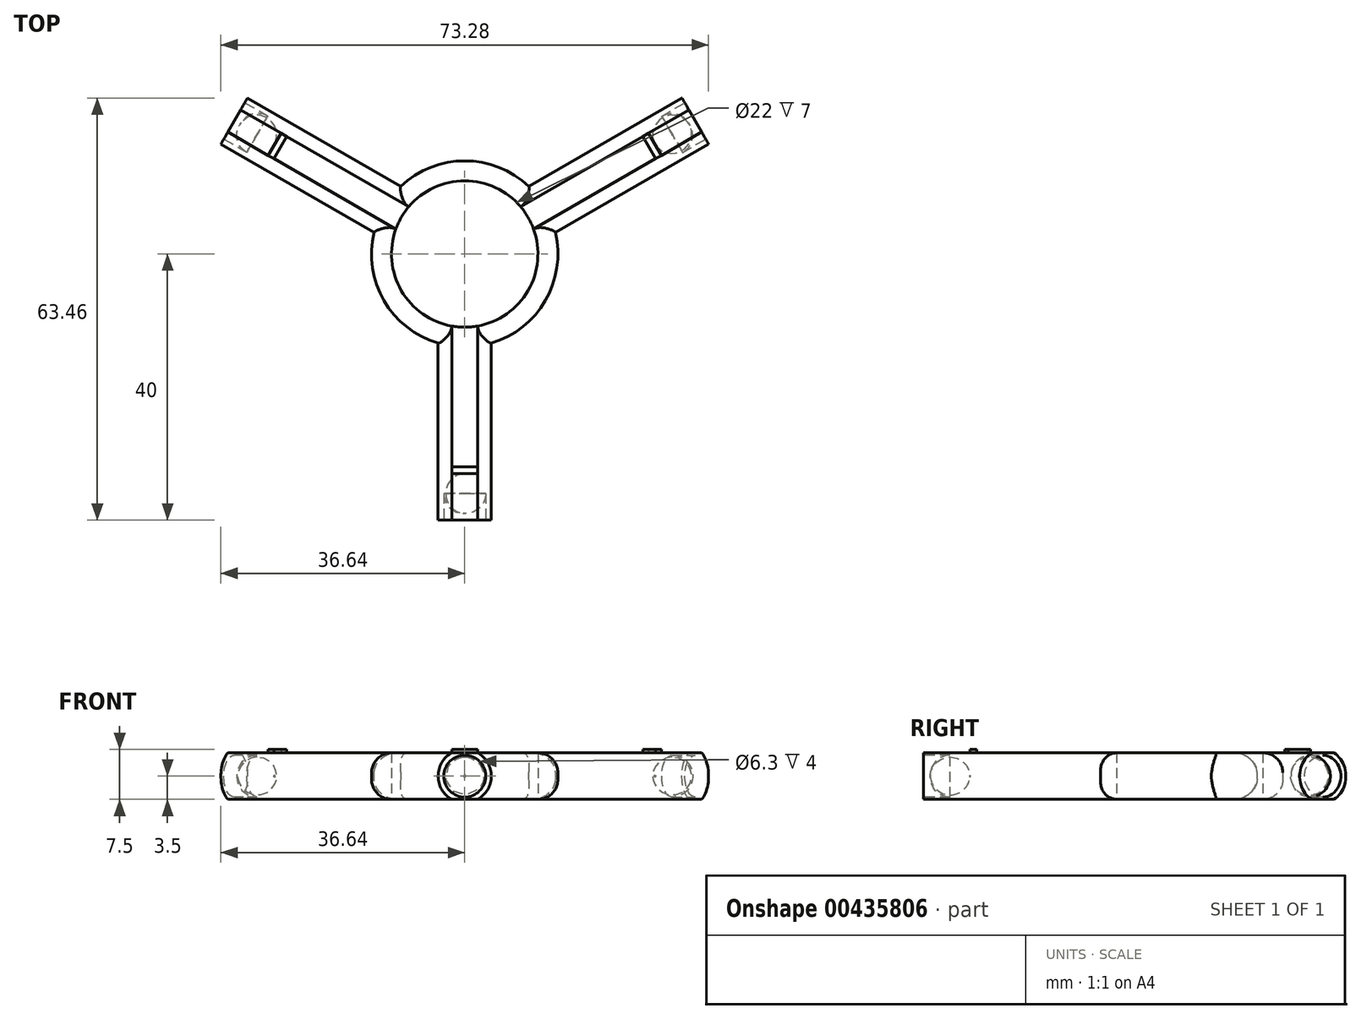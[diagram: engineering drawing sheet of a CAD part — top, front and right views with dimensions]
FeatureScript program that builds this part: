
annotation { "Feature Type Name" : "Feature", "Feature Type Description" : "" }
export const myFeature = defineFeature(function(context is Context, id is Id, definition is map)
    precondition{}
    {
        {
            var Q0;
            Q0=qCreatedBy(makeId("Top.planeOp"),FACE);
            var sketch = newSketch(context, id + "F0", { "sketchPlane" : qUnion([Q0])});
            skCircle(sketch, "E0", {"center": v(0, 0) * mm, "radius": 11 * mm});
            skCircle(sketch, "E1.0", {"center": v(0, 0) * mm, "radius": 14 * mm});
            skSolve(sketch);
        }
        {
            var Q0;
            Q0=makeQuery(id+"F0.imprint","IMPRINT",FACE,{"disambiguationData":[TD([[makeQuery(id+"F0.imprint","IMPRINT",EDGE,{"derivedFrom":sQuery(id+"F0.wireOp",EDGE,"E0")}),-1.0]])]});
            extrude(context, id + "F1", {"entities" : qUnion([Q0]), "depth" : 7 * mm, "offsetDistance" : 25 * mm});
        }
        {
            var Q0;
            Q0=qCreatedBy(makeId("Front.planeOp"),FACE);
            var sketch = newSketch(context, id + "F2", { "sketchPlane" : qUnion([Q0])});
            skCircle(sketch, "E2", {"center": v(0, 3.5) * mm, "radius": 4 * mm});
            skLineSegment(sketch, "E3", {"start": v(1.94, 7) * mm, "end": v(-1.94, 7) * mm});
            skLineSegment(sketch, "E4", {"start": v(1.94, 0) * mm, "end": v(-1.94, 0) * mm});
            skSolve(sketch);
        }
        {
            var Q0;
            {var subQ0=sQuery(id+"F2.wireOp",EDGE,"E3");Q0=makeQuery(id+"F2.imprint","IMPRINT",FACE,{"disambiguationData":[TD([[makeQuery(id+"F2.imprint","IMPRINT",EDGE,{"derivedFrom":subQ0}),1.0]])]});}
            extrude(context, id + "F3", {"entities" : qUnion([Q0]), "operationType" : NewBodyOperationType.ADD, "depth" : 40 * mm, "offsetDistance" : 25 * mm, "hasSecondDirection" : true, "secondDirectionBound" : SecondDirectionBoundingType.UP_TO_NEXT, "secondDirectionOppositeDirection" : false, "secondDirectionDepth" : 9.3 * mm});
        }
        {
            var Q0;
            Q0=makeQuery(id+"F3.opExtrude","CAP_FACE",FACE,{"disambiguationData":[OSD([sQuery(id+"F2.wireOp",EDGE,"E2"),sQuery(id+"F2.wireOp",EDGE,"E3"),sQuery(id+"F2.wireOp",EDGE,"E4")])],"isStart":false});
            var sketch = newSketch(context, id + "F4", { "sketchPlane" : qUnion([Q0])});
            skCircle(sketch, "E5", {"center": v(0, 3.5) * mm, "radius": 3.15 * mm});
            skCircle(sketch, "E6", {"center": v(0, 3.5) * mm, "radius": 4 * mm, "construction": true});
            skSolve(sketch);
        }
        {
            var Q0;
            Q0=makeQuery(id+"F4.imprint","IMPRINT",FACE,{"disambiguationData":[TD([[makeQuery(id+"F4.imprint","IMPRINT",EDGE,{"derivedFrom":sQuery(id+"F4.wireOp",EDGE,"E5")}),1.0]])]});
            extrude(context, id + "F5", {"entities" : qUnion([Q0]), "operationType" : NewBodyOperationType.REMOVE, "oppositeDirection" : true, "depth" : 7 * mm, "offsetDistance" : 25 * mm});
        }
        {
            var Q0;
            Q0=makeQuery(id+"F5.boolean.opBoolean","COPY",EDGE,{"derivedFrom":makeQuery(id+"F5.opExtrude","CAP_EDGE",EDGE,{"disambiguationData":[OSD([sQuery(id+"F4.wireOp",EDGE,"E5")])],"isStart":false})});
            var Q1;
            Q1=makeQuery(id+"F1.opExtrude","CAP_EDGE",EDGE,{"disambiguationData":[OSD([sQuery(id+"F0.wireOp",EDGE,"E1.0")])],"isStart":false});
            var Q2;
            Q2=makeQuery(id+"F1.opExtrude","CAP_EDGE",EDGE,{"disambiguationData":[OSD([sQuery(id+"F0.wireOp",EDGE,"E1.0")])],"isStart":true});
            fillet(context, id + "F6", {"entities" : qUnion([Q0, Q1, Q2]), "radius" : 3 * mm, "tangentPropagation" : true, "allowEdgeOverflow" : false});
        }
        {
            var Q0;
            Q0=makeQuery(id+"F3.boolean.opBoolean","MERGE",FACE,{"derivedFrom":[makeQuery(id+"F1.opExtrude","CAP_FACE",FACE,{"disambiguationData":[OSD([sQuery(id+"F0.wireOp",EDGE,"E0"),sQuery(id+"F0.wireOp",EDGE,"E1.0")])],"isStart":false}),makeQuery(id+"F3.opExtrude","SWEPT_FACE",FACE,{"disambiguationData":[OSD([sQuery(id+"F2.wireOp",EDGE,"E3")])]})]});
            var sketch = newSketch(context, id + "F7", { "sketchPlane" : qUnion([Q0])});
            skSolve(sketch);
        }
        {
            var Q0;
            {var subQ0=sQuery(id+"F2.wireOp",EDGE,"E3");Q0=makeQuery(id+"F7.imprint","IMPRINT",FACE,{"disambiguationData":[TD([[makeQuery(id+"F7.imprint","IMPRINT",EDGE,{"derivedFrom":makeQuery(id+"F3.opExtrude","CAP_EDGE",EDGE,{"disambiguationData":[OSD([subQ0])],"isStart":false})}),-1.0]])]});}
            var sketch = newSketch(context, id + "F8", { "sketchPlane" : qUnion([Q0])});
            skLineSegment(sketch, "E7.bottom", {"start": v(1.94, -32) * mm, "end": v(-1.94, -32) * mm});
            skLineSegment(sketch, "E7.top", {"start": v(1.94, -33) * mm, "end": v(-1.94, -33) * mm});
            skLineSegment(sketch, "E7.left", {"start": v(1.94, -32) * mm, "end": v(1.94, -33) * mm});
            skLineSegment(sketch, "E7.right", {"start": v(-1.94, -32) * mm, "end": v(-1.94, -33) * mm});
            skPoint(sketch, "E7.middle", {"position": v(0, -32.5) * mm});
            skSolve(sketch);
        }
        {
            var Q0;
            Q0=makeQuery(id+"F8.imprint","IMPRINT",FACE,{"disambiguationData":[TD([[makeQuery(id+"F8.imprint","IMPRINT",EDGE,{"derivedFrom":sQuery(id+"F8.wireOp",EDGE,"E7.bottom")}),1.0]])]});
            extrude(context, id + "F9", {"entities" : qUnion([Q0]), "operationType" : NewBodyOperationType.ADD, "depth" : 0.5 * mm, "offsetDistance" : 25 * mm});
        }
        {
            var Q0;
            Q0=makeQuery(id+"F1.opExtrude","SWEPT_BODY",BODY,{"disambiguationData":[OSD([sQuery(id+"F0.wireOp",EDGE,"E0"),sQuery(id+"F0.wireOp",EDGE,"E1.0")])]});
            var Q1;
            Q1=makeQuery(id+"F1.opExtrude","CAP_EDGE",EDGE,{"disambiguationData":[OSD([sQuery(id+"F0.wireOp",EDGE,"E0")])],"isStart":false});
            circularPattern(context, id + "F10", {"operationType" : NewBodyOperationType.ADD, "entities" : qUnion([Q0]), "axis" : qUnion([Q1]), "angle" : 360 * degree, "instanceCount" : 3, "equalSpace" : true});
        }
    });
